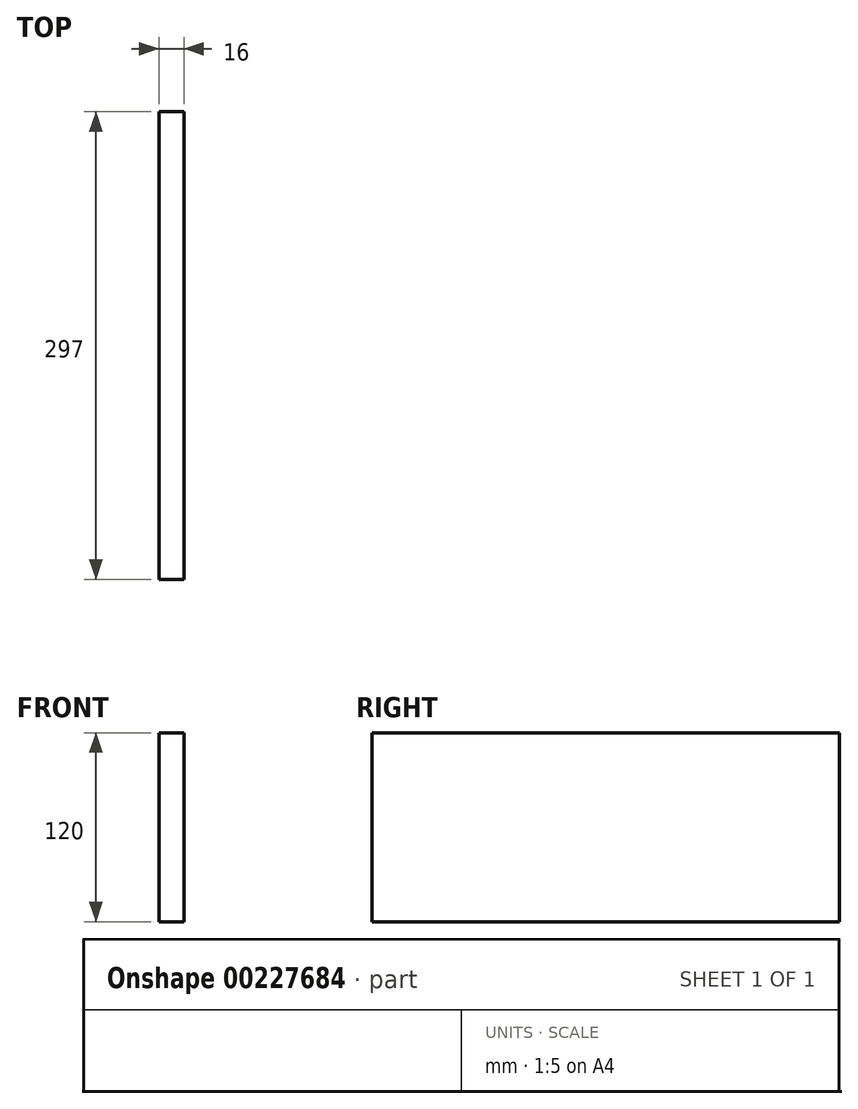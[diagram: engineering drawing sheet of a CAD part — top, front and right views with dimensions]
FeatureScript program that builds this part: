
annotation { "Feature Type Name" : "Feature", "Feature Type Description" : "" }
export const myFeature = defineFeature(function(context is Context, id is Id, definition is map)
    precondition{}
    {
        {
            var Q0;
            Q0=qCreatedBy(makeId("Right.planeOp"),FACE);
            var sketch = newSketch(context, id + "F0", { "sketchPlane" : qUnion([Q0])});
            skLineSegment(sketch, "E0.bottom", {"start": v(148.5, -60) * mm, "end": v(-148.5, -60) * mm});
            skLineSegment(sketch, "E0.top", {"start": v(148.5, 60) * mm, "end": v(-148.5, 60) * mm});
            skLineSegment(sketch, "E0.left", {"start": v(148.5, -60) * mm, "end": v(148.5, 60) * mm});
            skLineSegment(sketch, "E0.right", {"start": v(-148.5, -60) * mm, "end": v(-148.5, 60) * mm});
            skPoint(sketch, "E0.middle", {"position": v(0, 0) * mm});
            skSolve(sketch);
        }
        {
            var Q0;
            Q0=qSketchRegion(id+"F0",true);
            extrude(context, id + "F1", {"entities" : qUnion([Q0]), "depth" : 16 * mm, "symmetric" : true});
        }
    });
